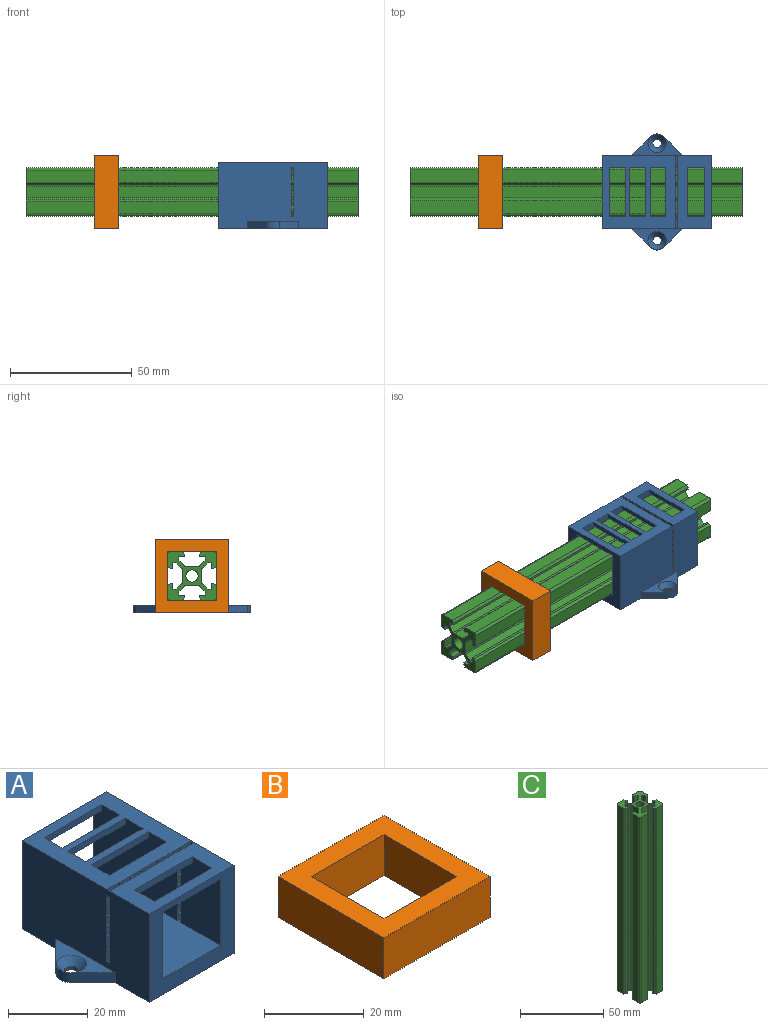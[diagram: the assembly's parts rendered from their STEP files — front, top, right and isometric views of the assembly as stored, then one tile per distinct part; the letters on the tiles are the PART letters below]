
ASSEMBLY  parts=3 mates=2
PART A: 118 faces, bbox 47.8x45x27 mm
  f0: plane 4.85x2.7mm, normal (0,-1,0), area 13.1mm2, adj f37,f59,f105,f116
  f1: plane 4.85x2.7mm, normal (0,1,0), area 13.1mm2, adj f37,f59,f105,f116
  f2: plane 8x1.93mm, normal (0,-1,0), area 14.1mm2, adj f37,f38,f39,f59,f96,f97,f98,f101
  f3: plane 8x1.93mm, normal (0,1,0), area 14.1mm2, adj f37,f38,f39,f59,f96,f97,f98,f101
  f4: plane 4.85x2.7mm, normal (0,-1,0), area 13.1mm2, adj f37,f59,f111,f112
  f5: plane 4.85x2.7mm, normal (0,1,0), area 13.1mm2, adj f37,f59,f111,f112
  f6: plane 4.85x2.7mm, normal (0,-1,0), area 13.1mm2, adj f37,f59,f110,f117
  f7: plane 4.85x2.7mm, normal (0,1,0), area 13.1mm2, adj f37,f59,f110,f117
  f8: plane 4.85x2.7mm, normal (0,-1,0), area 13.1mm2, adj f37,f59,f108,f113
  f9: plane 4.85x2.7mm, normal (0,1,0), area 13.1mm2, adj f37,f59,f108,f113
  f10: plane 3.7x1.85mm, normal (0,-1,0), area 6.8mm2, adj f38,f39,f107,f114
  f11: plane 3.7x1.85mm, normal (0,1,0), area 6.8mm2, adj f38,f39,f107,f114
  f12: plane 4.85x2.7mm, normal (0,-1,0), area 13.1mm2, adj f37,f59,f100,f104
  f13: plane 4.85x2.7mm, normal (0,1,0), area 13.1mm2, adj f37,f59,f100,f104
  f14: plane 5.4x1.85mm, normal (0,-1,0), area 10mm2, adj f38,f39,f94,f106
  f15: plane 4.85x1.93mm, normal (0,-1,0), area 9.3mm2, adj f37,f58,f59,f99
  f16: plane 4.85x1.93mm, normal (0,1,0), area 9.3mm2, adj f37,f58,f59,f99
  f17: plane 4.85x2.7mm, normal (0,-1,0), area 13.1mm2, adj f37,f59,f95,f109
  f18: plane 4.85x2.7mm, normal (0,1,0), area 13.1mm2, adj f37,f59,f95,f109
  f19: plane 5.4x1.85mm, normal (0,1,0), area 10mm2, adj f38,f39,f94,f106
  f20: plane 3.7x1.85mm, normal (0,-1,0), area 6.8mm2, adj f38,f39,f92,f93
  f21: plane 3.7x1.85mm, normal (0,1,0), area 6.8mm2, adj f38,f39,f92,f93
  f22: plane 8x1.93mm, normal (0,-1,0), area 14.1mm2, adj f36,f38,f39,f57,f85,f86,f87,f88
  f23: plane 8x1.93mm, normal (0,1,0), area 14.1mm2, adj f36,f38,f39,f57,f85,f86,f87,f88
  f24: plane 4.85x2.7mm, normal (0,-1,0), area 13.1mm2, adj f36,f57,f83,f84
  f25: plane 4.85x2.7mm, normal (0,1,0), area 13.1mm2, adj f36,f57,f83,f84
  f26: plane 4.85x2.7mm, normal (0,-1,0), area 13.1mm2, adj f36,f57,f81,f82
  f27: plane 4.85x2.7mm, normal (0,1,0), area 13.1mm2, adj f36,f57,f81,f82
  f28: plane 4.85x2.7mm, normal (0,-1,0), area 13.1mm2, adj f36,f57,f79,f80
  f29: plane 4.85x2.7mm, normal (0,1,0), area 13.1mm2, adj f36,f57,f79,f80
  f30: plane 4.85x2.7mm, normal (0,-1,0), area 13.1mm2, adj f36,f57,f77,f78
  f31: plane 4.85x2.7mm, normal (0,1,0), area 13.1mm2, adj f36,f57,f77,f78
  f32: plane 4.85x2.7mm, normal (0,-1,0), area 13.1mm2, adj f36,f57,f75,f76
  f33: plane 4.85x2.7mm, normal (0,1,0), area 13.1mm2, adj f36,f57,f75,f76
  f34: plane 4.85x2.7mm, normal (0,-1,0), area 13.1mm2, adj f36,f57,f73,f74
  f35: plane 4.85x2.7mm, normal (0,1,0), area 13.1mm2, adj f36,f57,f73,f74
  f36: plane 45x27mm, normal (-1,0,0), area 1133.8mm2, adj f22,f23,f24,f25,f26,f27,f28,f29
  f37: plane 45x27mm, normal (1,0,0), area 1133.8mm2, adj f0,f1,f2,f3,f4,f5,f6,f7
  f38: plane 45x30mm, normal (0,0,1), area 794.6mm2, adj f2,f3,f10,f11,f14,f19,f20,f21
  f39: plane 20.3x9mm, normal (0,0,-1), area 163.6mm2, adj f2,f3,f10,f11,f14,f19,f20,f21
  f40: plane 20.3x3mm, normal (0,0,-1), area 60.9mm2, adj f43,f57,f59,f66
  f41: plane 20.3x2mm, normal (0,0,-1), area 40.6mm2, adj f57,f59,f65,f67
  f42: plane 20.3x2mm, normal (0,0,-1), area 40.6mm2, adj f57,f59,f62,f64
  f43: plane 30x27mm, normal (0,1,0), area 397.9mm2, adj f36,f37,f38,f40,f45,f57,f58,f59
  f44: plane 30x27mm, normal (0,-1,0), area 397.9mm2, adj f36,f37,f38,f45,f56,f57,f58,f59
  f45: plane 47.77x45mm, normal (0,0,-1), area 1544.5mm2, adj f36,f37,f43,f44,f46,f47,f48,f49
  f46: plane 7.75x7.75mm, normal (-0.71,0.71,0), area 32.9mm2, adj f36,f45,f47,f50
  f47: cylinder r=3.88mm len=5.49mm, axis (0,0,-1), area 18.3mm2, adj f45,f46,f49,f50
  f48: cylinder r=1.75mm len=3.5mm, axis (0,0,-1), area 11mm2, adj f45,f70
  f49: plane 7.75x7.75mm, normal (-0.71,-0.71,0), area 32.9mm2, adj f36,f45,f47,f50
  f50: plane 20.98x8.88mm, normal (0,0,1), area 62.7mm2, adj f36,f46,f47,f49,f70
  f51: plane 7.75x7.75mm, normal (0.71,0.71,0), area 32.9mm2, adj f37,f45,f54,f55
  f52: plane 7.75x7.75mm, normal (0.71,-0.71,0), area 32.9mm2, adj f37,f45,f54,f55
  f53: cylinder r=1.75mm len=3.5mm, axis (0,0,-1), area 11mm2, adj f45,f71
  f54: cylinder r=3.88mm len=5.49mm, axis (0,0,-1), area 18.3mm2, adj f45,f51,f52,f55
  f55: plane 20.98x8.88mm, normal (0,0,1), area 62.7mm2, adj f37,f51,f52,f54,f71
  f56: plane 20.3x3mm, normal (0,0,-1), area 60.9mm2, adj f44,f57,f59,f69
  f57: plane 45x22.15mm, normal (1,0,0), area 943.4mm2, adj f22,f23,f24,f25,f26,f27,f28,f29
  f58: plane 45x30mm, normal (0,0,1), area 923.2mm2, adj f15,f16,f36,f37,f43,f44,f57,f59
  f59: plane 45x22.15mm, normal (-1,0,0), area 943.4mm2, adj f0,f1,f2,f3,f4,f5,f6,f7
  f60: plane 4.85x1.93mm, normal (0,-1,0), area 9.3mm2, adj f36,f57,f58,f72
  f61: plane 4.85x1.93mm, normal (0,1,0), area 9.3mm2, adj f36,f57,f58,f72
  f62: plane 20.3x1.85mm, normal (0,-1,0), area 37.6mm2, adj f38,f42,f57,f59
  f63: plane 20.3x1.85mm, normal (0,1,0), area 37.6mm2, adj f38,f39,f57,f59
  f64: plane 20.3x1.85mm, normal (0,1,0), area 37.6mm2, adj f38,f42,f57,f59
  f65: plane 20.3x1.85mm, normal (0,-1,0), area 37.6mm2, adj f38,f41,f57,f59
  f66: plane 20.3x1.85mm, normal (0,-1,0), area 37.6mm2, adj f38,f40,f57,f59
  f67: plane 20.3x1.85mm, normal (0,1,0), area 37.6mm2, adj f38,f41,f57,f59
  f68: plane 20.3x1.85mm, normal (0,-1,0), area 37.6mm2, adj f38,f39,f57,f59
  f69: plane 20.3x1.85mm, normal (0,1,0), area 37.6mm2, adj f38,f56,f57,f59
  f70: cone r=1.75mm half-angle=45deg, axis (0,0,1), area 48.9mm2, adj f48,f50
  f71: cone r=3.75mm half-angle=45deg, axis (0,0,1), area 48.9mm2, adj f53,f55
  f72: plane 4.85x1mm, normal (0,0,-1), area 4.9mm2, adj f36,f57,f60,f61
  f73: plane 4.85x1mm, normal (0,0,1), area 4.9mm2, adj f34,f35,f36,f57
  f74: plane 4.85x1mm, normal (0,0,-1), area 4.9mm2, adj f34,f35,f36,f57
  f75: plane 4.85x1mm, normal (0,0,1), area 4.9mm2, adj f32,f33,f36,f57
  f76: plane 4.85x1mm, normal (0,0,-1), area 4.9mm2, adj f32,f33,f36,f57
  f77: plane 4.85x1mm, normal (0,0,1), area 4.9mm2, adj f30,f31,f36,f57
  f78: plane 4.85x1mm, normal (0,0,-1), area 4.9mm2, adj f30,f31,f36,f57
  f79: plane 4.85x1mm, normal (0,0,1), area 4.9mm2, adj f28,f29,f36,f57
  f80: plane 4.85x1mm, normal (0,0,-1), area 4.9mm2, adj f28,f29,f36,f57
  f81: plane 4.85x1mm, normal (0,0,1), area 4.9mm2, adj f26,f27,f36,f57
  f82: plane 4.85x1mm, normal (0,0,-1), area 4.9mm2, adj f26,f27,f36,f57
  f83: plane 4.85x1mm, normal (0,0,1), area 4.9mm2, adj f24,f25,f36,f57
  f84: plane 4.85x1mm, normal (0,0,-1), area 4.9mm2, adj f24,f25,f36,f57
  f85: plane 4.85x1mm, normal (0,0,1), area 4.9mm2, adj f22,f23,f36,f57
  f86: plane 1.85x1mm, normal (1,0,0), area 1.9mm2, adj f22,f23,f38,f87
  f87: plane 1x0.3mm, normal (0,0,-1), area 0.3mm2, adj f22,f23,f36,f86
  f88: plane 1.85x1mm, normal (1,0,0), area 1.9mm2, adj f22,f23,f38,f90
  f89: plane 1.85x1mm, normal (-1,0,0), area 1.9mm2, adj f22,f23,f38,f90
  f90: plane 1x0.3mm, normal (0,0,-1), area 0.3mm2, adj f22,f23,f88,f89
  f91: plane 1.85x1mm, normal (-1,0,0), area 1.9mm2, adj f22,f23,f38,f39
  f92: plane 1.85x1mm, normal (1,0,0), area 1.9mm2, adj f20,f21,f38,f39
  f93: plane 1.85x1mm, normal (-1,0,0), area 1.9mm2, adj f20,f21,f38,f39
  f94: plane 1.85x1mm, normal (1,0,0), area 1.9mm2, adj f14,f19,f38,f39
  f95: plane 4.85x1mm, normal (0,0,-1), area 4.9mm2, adj f17,f18,f37,f59
  f96: plane 4.85x1mm, normal (0,0,1), area 4.9mm2, adj f2,f3,f37,f59
  f97: plane 1.85x1mm, normal (-1,0,0), area 1.9mm2, adj f2,f3,f38,f98
  f98: plane 1x0.3mm, normal (0,0,-1), area 0.3mm2, adj f2,f3,f37,f97
  f99: plane 4.85x1mm, normal (0,0,-1), area 4.9mm2, adj f15,f16,f37,f59
  f100: plane 4.85x1mm, normal (0,0,1), area 4.9mm2, adj f12,f13,f37,f59
  f101: plane 1.85x1mm, normal (-1,0,0), area 1.9mm2, adj f2,f3,f38,f103
  f102: plane 1.85x1mm, normal (1,0,0), area 1.9mm2, adj f2,f3,f38,f103
  f103: plane 1x0.3mm, normal (0,0,-1), area 0.3mm2, adj f2,f3,f101,f102
  f104: plane 4.85x1mm, normal (0,0,-1), area 4.9mm2, adj f12,f13,f37,f59
  f105: plane 4.85x1mm, normal (0,0,1), area 4.9mm2, adj f0,f1,f37,f59
  f106: plane 1.85x1mm, normal (-1,0,0), area 1.9mm2, adj f14,f19,f38,f39
  f107: plane 1.85x1mm, normal (1,0,0), area 1.9mm2, adj f10,f11,f38,f39
  f108: plane 4.85x1mm, normal (0,0,-1), area 4.9mm2, adj f8,f9,f37,f59
  f109: plane 4.85x1mm, normal (0,0,1), area 4.9mm2, adj f17,f18,f37,f59
  f110: plane 4.85x1mm, normal (0,0,-1), area 4.9mm2, adj f6,f7,f37,f59
  f111: plane 4.85x1mm, normal (0,0,1), area 4.9mm2, adj f4,f5,f37,f59
  f112: plane 4.85x1mm, normal (0,0,-1), area 4.9mm2, adj f4,f5,f37,f59
  f113: plane 4.85x1mm, normal (0,0,1), area 4.9mm2, adj f8,f9,f37,f59
  f114: plane 1.85x1mm, normal (-1,0,0), area 1.9mm2, adj f10,f11,f38,f39
  f115: plane 1.85x1mm, normal (1,0,0), area 1.9mm2, adj f2,f3,f38,f39
  f116: plane 4.85x1mm, normal (0,0,-1), area 4.9mm2, adj f0,f1,f37,f59
  f117: plane 4.85x1mm, normal (0,0,1), area 4.9mm2, adj f6,f7,f37,f59
PART B: 10 faces, bbox 30x30x10 mm
  f0: plane 30x10mm, normal (1,0,0), area 300mm2, adj f1,f7,f8,f9
  f1: plane 30x10mm, normal (0,1,0), area 300mm2, adj f0,f2,f8,f9
  f2: plane 30x10mm, normal (-1,0,0), area 300mm2, adj f1,f7,f8,f9
  f3: plane 20.5x10mm, normal (-1,0,0), area 205mm2, adj f4,f6,f8,f9
  f4: plane 20.5x10mm, normal (0,1,0), area 205mm2, adj f3,f5,f8,f9
  f5: plane 20.5x10mm, normal (1,0,0), area 205mm2, adj f4,f6,f8,f9
  f6: plane 20.5x10mm, normal (0,-1,0), area 205mm2, adj f3,f5,f8,f9
  f7: plane 30x10mm, normal (0,-1,0), area 300mm2, adj f0,f2,f8,f9
  f8: plane 30x30mm, normal (0,0,1), area 479.8mm2, adj f0,f1,f2,f3,f4,f5,f6,f7
  f9: plane 30x30mm, normal (0,0,-1), area 479.7mm2, adj f0,f1,f2,f3,f4,f5,f6,f7
PART C: 75 faces, bbox 20x20x136.4 mm
  f0: plane 136.4x1mm, normal (1,0,0), area 136.4mm2, adj f1,f71,f73,f74
  f1: plane 136.4x1mm, normal (0.82,0.57,0), area 166.5mm2, adj f0,f2,f73,f74
  f2: plane 136.4x5.3mm, normal (0,1,0), area 722.9mm2, adj f1,f3,f73,f74
  f3: cylinder r=1mm len=136.4mm, axis (0,0,-1), area 214.3mm2, adj f2,f4,f73,f74
  f4: plane 136.4x5.3mm, normal (-1,0,0), area 722.9mm2, adj f3,f5,f73,f74
  f5: plane 136.4x1mm, normal (-0.57,-0.82,0), area 166.5mm2, adj f4,f6,f73,f74
  f6: plane 136.4x1mm, normal (0,-1,0), area 136.4mm2, adj f5,f7,f73,f74
  f7: plane 136.4x2.5mm, normal (1,0,0), area 341mm2, adj f6,f8,f73,f74
  f8: plane 136.4x1.23mm, normal (0,-1,0), area 168.1mm2, adj f7,f9,f73,f74
  f9: cylinder r=0.5mm len=136.4mm, axis (0,0,-1), area 53.6mm2, adj f8,f10,f73,f74
  f10: plane 136.4x2.22mm, normal (-0.71,-0.71,0), area 428.5mm2, adj f9,f11,f73,f74
  f11: cylinder r=1mm len=136.4mm, axis (0,0,-1), area 107.1mm2, adj f10,f12,f73,f74
  f12: plane 136.4x4.85mm, normal (-1,0,0), area 661.6mm2, adj f11,f13,f73,f74
  f13: cylinder r=1mm len=136.4mm, axis (0,0,-1), area 107.1mm2, adj f12,f14,f73,f74
  f14: plane 136.4x2.22mm, normal (-0.71,0.71,0), area 428.5mm2, adj f13,f15,f73,f74
  f15: cylinder r=0.5mm len=136.4mm, axis (0,0,-1), area 53.6mm2, adj f14,f16,f73,f74
  f16: plane 136.4x1.23mm, normal (0,1,0), area 168.1mm2, adj f15,f17,f73,f74
  f17: plane 136.4x2.5mm, normal (1,0,0), area 341mm2, adj f16,f18,f73,f74
  f18: plane 136.4x1mm, normal (0,1,0), area 136.4mm2, adj f17,f19,f73,f74
  f19: plane 136.4x1mm, normal (-0.57,0.82,0), area 166.5mm2, adj f18,f20,f73,f74
  f20: plane 136.4x5.3mm, normal (-1,0,0), area 722.9mm2, adj f19,f21,f73,f74
  f21: cylinder r=1mm len=136.4mm, axis (0,0,-1), area 214.3mm2, adj f20,f22,f73,f74
  f22: plane 136.4x5.3mm, normal (0,-1,0), area 722.9mm2, adj f21,f23,f73,f74
  f23: plane 136.4x1mm, normal (0.82,-0.57,0), area 166.5mm2, adj f22,f24,f73,f74
  f24: plane 136.4x1mm, normal (1,0,0), area 136.4mm2, adj f23,f25,f73,f74
  f25: plane 136.4x2.5mm, normal (0,1,0), area 341mm2, adj f24,f26,f73,f74
  f26: plane 136.4x1.23mm, normal (1,0,0), area 168.1mm2, adj f25,f27,f73,f74
  f27: cylinder r=0.5mm len=136.4mm, axis (0,0,-1), area 53.6mm2, adj f26,f28,f73,f74
  f28: plane 136.4x2.22mm, normal (0.71,-0.71,0), area 428.5mm2, adj f27,f29,f73,f74
  f29: cylinder r=1mm len=136.4mm, axis (0,0,-1), area 107.1mm2, adj f28,f30,f73,f74
  f30: plane 136.4x4.85mm, normal (0,-1,0), area 661.6mm2, adj f29,f31,f73,f74
  f31: cylinder r=1mm len=136.4mm, axis (0,0,-1), area 107.1mm2, adj f30,f32,f73,f74
  f32: plane 136.4x2.22mm, normal (-0.71,-0.71,0), area 428.5mm2, adj f31,f33,f73,f74
  f33: cylinder r=0.5mm len=136.4mm, axis (0,0,-1), area 53.6mm2, adj f32,f34,f73,f74
  f34: plane 136.4x1.23mm, normal (-1,0,0), area 168.1mm2, adj f33,f35,f73,f74
  f35: plane 136.4x2.5mm, normal (0,1,0), area 341mm2, adj f34,f36,f73,f74
  f36: plane 136.4x1mm, normal (-1,0,0), area 136.4mm2, adj f35,f37,f73,f74
  f37: plane 136.4x1mm, normal (-0.82,-0.57,0), area 166.5mm2, adj f36,f38,f73,f74
  f38: plane 136.4x5.3mm, normal (0,-1,0), area 722.9mm2, adj f37,f39,f73,f74
  f39: cylinder r=1mm len=136.4mm, axis (0,0,-1), area 214.3mm2, adj f38,f40,f73,f74
  f40: plane 136.4x5.3mm, normal (1,0,0), area 722.9mm2, adj f39,f41,f73,f74
  f41: plane 136.4x1mm, normal (0.57,0.82,0), area 166.5mm2, adj f40,f42,f73,f74
  f42: plane 136.4x1mm, normal (0,1,0), area 136.4mm2, adj f41,f43,f73,f74
  f43: plane 136.4x2.5mm, normal (-1,0,0), area 341mm2, adj f42,f44,f73,f74
  f44: plane 136.4x1.23mm, normal (0,1,0), area 168.1mm2, adj f43,f45,f73,f74
  f45: cylinder r=0.5mm len=136.4mm, axis (0,0,-1), area 53.6mm2, adj f44,f46,f73,f74
  f46: plane 136.4x2.22mm, normal (0.71,0.71,0), area 428.5mm2, adj f45,f47,f73,f74
  f47: cylinder r=1mm len=136.4mm, axis (0,0,-1), area 107.1mm2, adj f46,f48,f73,f74
  f48: plane 136.4x4.85mm, normal (1,0,0), area 661.6mm2, adj f47,f49,f73,f74
  f49: cylinder r=1mm len=136.4mm, axis (0,0,-1), area 107.1mm2, adj f48,f50,f73,f74
  f50: plane 136.4x2.22mm, normal (0.71,-0.71,0), area 428.5mm2, adj f49,f51,f73,f74
  f51: cylinder r=0.5mm len=136.4mm, axis (0,0,-1), area 53.6mm2, adj f50,f52,f73,f74
  f52: plane 136.4x1.23mm, normal (0,-1,0), area 168.1mm2, adj f51,f53,f73,f74
  f53: plane 136.4x2.5mm, normal (-1,0,0), area 341mm2, adj f52,f54,f73,f74
  f54: plane 136.4x1mm, normal (0,-1,0), area 136.4mm2, adj f53,f55,f73,f74
  f55: plane 136.4x1mm, normal (0.57,-0.82,0), area 166.5mm2, adj f54,f56,f73,f74
  f56: plane 136.4x5.3mm, normal (1,0,0), area 722.9mm2, adj f55,f57,f73,f74
  f57: cylinder r=1mm len=136.4mm, axis (0,0,-1), area 214.3mm2, adj f56,f58,f73,f74
  f58: plane 136.4x5.3mm, normal (0,1,0), area 722.9mm2, adj f57,f59,f73,f74
  f59: plane 136.4x1mm, normal (-0.82,0.57,0), area 166.5mm2, adj f58,f60,f73,f74
  f60: plane 136.4x1mm, normal (-1,0,0), area 136.4mm2, adj f59,f61,f73,f74
  f61: plane 136.4x2.5mm, normal (0,-1,0), area 341mm2, adj f60,f62,f73,f74
  f62: plane 136.4x1.23mm, normal (-1,0,0), area 168.1mm2, adj f61,f63,f73,f74
  f63: cylinder r=0.5mm len=136.4mm, axis (0,0,-1), area 53.6mm2, adj f62,f64,f73,f74
  f64: plane 136.4x2.22mm, normal (-0.71,0.71,0), area 428.5mm2, adj f63,f65,f73,f74
  f65: cylinder r=1mm len=136.4mm, axis (0,0,-1), area 107.1mm2, adj f64,f66,f73,f74
  f66: plane 136.4x4.85mm, normal (0,1,0), area 661.6mm2, adj f65,f67,f73,f74
  f67: cylinder r=1mm len=136.4mm, axis (0,0,-1), area 107.1mm2, adj f66,f68,f73,f74
  f68: plane 136.4x2.22mm, normal (0.71,0.71,0), area 428.5mm2, adj f67,f69,f73,f74
  f69: cylinder r=0.5mm len=136.4mm, axis (0,0,-1), area 53.6mm2, adj f68,f70,f73,f74
  f70: plane 136.4x1.23mm, normal (1,0,0), area 168.1mm2, adj f69,f71,f73,f74
  f71: plane 136.4x2.5mm, normal (0,-1,0), area 341mm2, adj f0,f70,f73,f74
  f72: cylinder r=2.5mm len=136.4mm, axis (0,0,-1), area 2142.6mm2, adj f73,f74
  f73: plane 20x20mm, normal (0,0,1), area 176.8mm2, adj f0,f1,f2,f3,f4,f5,f6,f7
  f74: plane 20x20mm, normal (0,0,-1), area 176.8mm2, adj f0,f1,f2,f3,f4,f5,f6,f7
PLACE A rot(axis=(0,0,1),90deg) t=(-38.5,1.57,82.3)mm fixed
PLACE B rot(axis=(-0.58,-0.58,0.58),120deg) t=(-104.06,-52.91,97.3)mm
PLACE C rot(axis=(0,1,0),90deg) t=(-142.26,-52.91,122.3)mm
MATE slider C.f72 <-> A.f44  axis (1,0,0) through (-5.86,-52.91,97.3)mm
MATE fastened B.f8 <-> C.f72  axis (-1,0,0) through (-114.06,-52.91,97.3)mm
